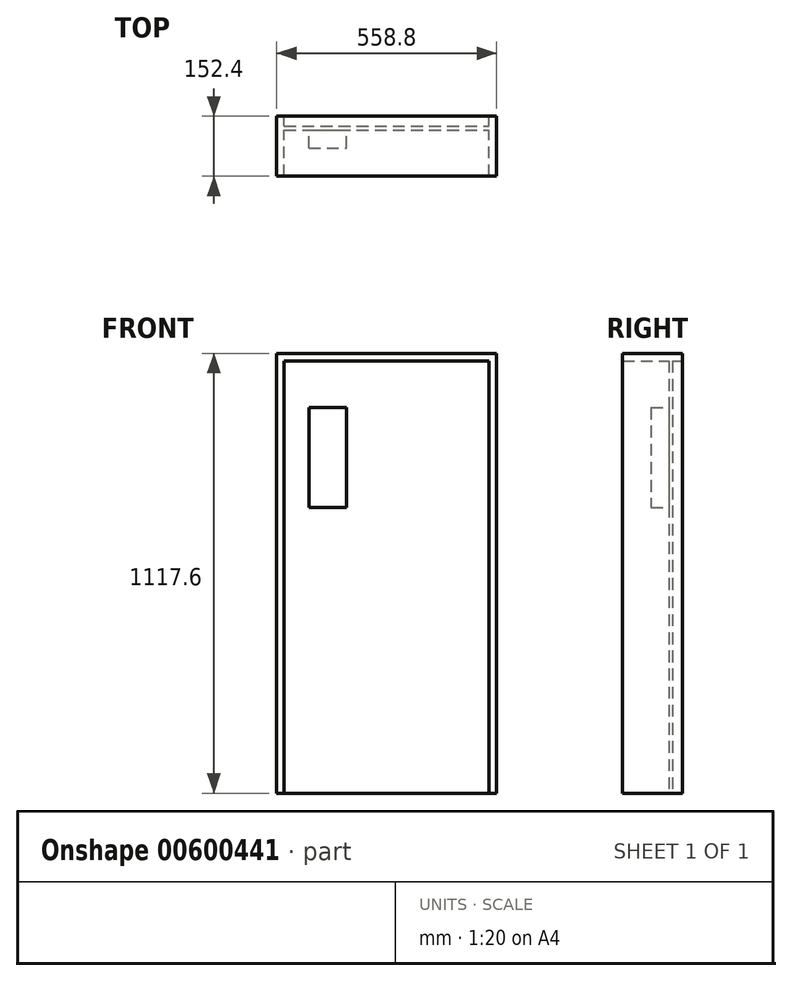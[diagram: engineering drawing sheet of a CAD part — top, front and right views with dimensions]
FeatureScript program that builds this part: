
annotation { "Feature Type Name" : "Feature", "Feature Type Description" : "" }
export const myFeature = defineFeature(function(context is Context, id is Id, definition is map)
    precondition{}
    {
        {
            var Q0;
            Q0=qCreatedBy(makeId("Front.planeOp"),FACE);
            var sketch = newSketch(context, id + "F0", { "sketchPlane" : qUnion([Q0])});
            skLineSegment(sketch, "E0.bottom", {"start": v(-299.58, 656.2) * mm, "end": v(259.22, 656.2) * mm});
            skLineSegment(sketch, "E0.top", {"start": v(-299.58, -461.4) * mm, "end": v(259.22, -461.4) * mm});
            skLineSegment(sketch, "E0.left", {"start": v(-299.58, 656.2) * mm, "end": v(-299.58, -461.4) * mm});
            skLineSegment(sketch, "E0.right", {"start": v(259.22, 656.2) * mm, "end": v(259.22, -461.4) * mm});
            skLineSegment(sketch, "E1.0", {"start": v(-280.53, 637.15) * mm, "end": v(240.17, 637.15) * mm});
            skLineSegment(sketch, "E1.1", {"start": v(-280.53, 637.15) * mm, "end": v(-280.53, -461.4) * mm});
            skLineSegment(sketch, "E1.3", {"start": v(240.17, 637.15) * mm, "end": v(240.17, -461.4) * mm});
            skSolve(sketch);
        }
        {
            var Q0;
            Q0=makeQuery(id+"F0.imprint","IMPRINT",FACE,{"disambiguationData":[TD([[makeQuery(id+"F0.imprint","IMPRINT",EDGE,{"derivedFrom":sQuery(id+"F0.wireOp",EDGE,"E0.bottom")}),-1.0]])]});
            extrude(context, id + "F1", {"entities" : qUnion([Q0]), "depth" : 152.4 * mm, "offsetDistance" : 25.4 * mm});
        }
        {
            var Q0;
            Q0=makeQuery(id+"F0.imprint","IMPRINT",FACE,{"disambiguationData":[TD([[makeQuery(id+"F0.imprint","IMPRINT",EDGE,{"derivedFrom":sQuery(id+"F0.wireOp",EDGE,"E1.0")}),-1.0]])]});
            extrude(context, id + "F2", {"entities" : qUnion([Q0]), "operationType" : NewBodyOperationType.ADD, "depth" : 34.92 * mm, "offsetDistance" : 25.4 * mm, "hasSecondDirection" : true, "secondDirectionOppositeDirection" : false, "secondDirectionDepth" : 25.4 * mm});
        }
        {
            var Q0;
            Q0=makeQuery(id+"F2.opExtrude","CAP_FACE",FACE,{"disambiguationData":[OSD([sQuery(id+"F0.wireOp",EDGE,"E0.top"),sQuery(id+"F0.wireOp",EDGE,"E1.0"),sQuery(id+"F0.wireOp",EDGE,"E1.1"),sQuery(id+"F0.wireOp",EDGE,"E1.3")])],"isStart":false});
            var sketch = newSketch(context, id + "F3", { "sketchPlane" : qUnion([Q0])});
            skLineSegment(sketch, "E2.bottom", {"start": v(-218.29, 518.36) * mm, "end": v(-123.04, 518.36) * mm});
            skLineSegment(sketch, "E2.top", {"start": v(-218.29, 264.36) * mm, "end": v(-123.04, 264.36) * mm});
            skLineSegment(sketch, "E2.left", {"start": v(-218.29, 518.36) * mm, "end": v(-218.29, 264.36) * mm});
            skLineSegment(sketch, "E2.right", {"start": v(-123.04, 518.36) * mm, "end": v(-123.04, 264.36) * mm});
            skSolve(sketch);
        }
        {
            var Q0;
            Q0=makeQuery(id+"F3.imprint","IMPRINT",FACE,{"disambiguationData":[TD([[makeQuery(id+"F3.imprint","IMPRINT",EDGE,{"derivedFrom":sQuery(id+"F3.wireOp",EDGE,"E2.bottom")}),-1.0]])]});
            extrude(context, id + "F4", {"entities" : qUnion([Q0]), "operationType" : NewBodyOperationType.ADD, "depth" : 45.72 * mm, "offsetDistance" : 25.4 * mm});
        }
    });
